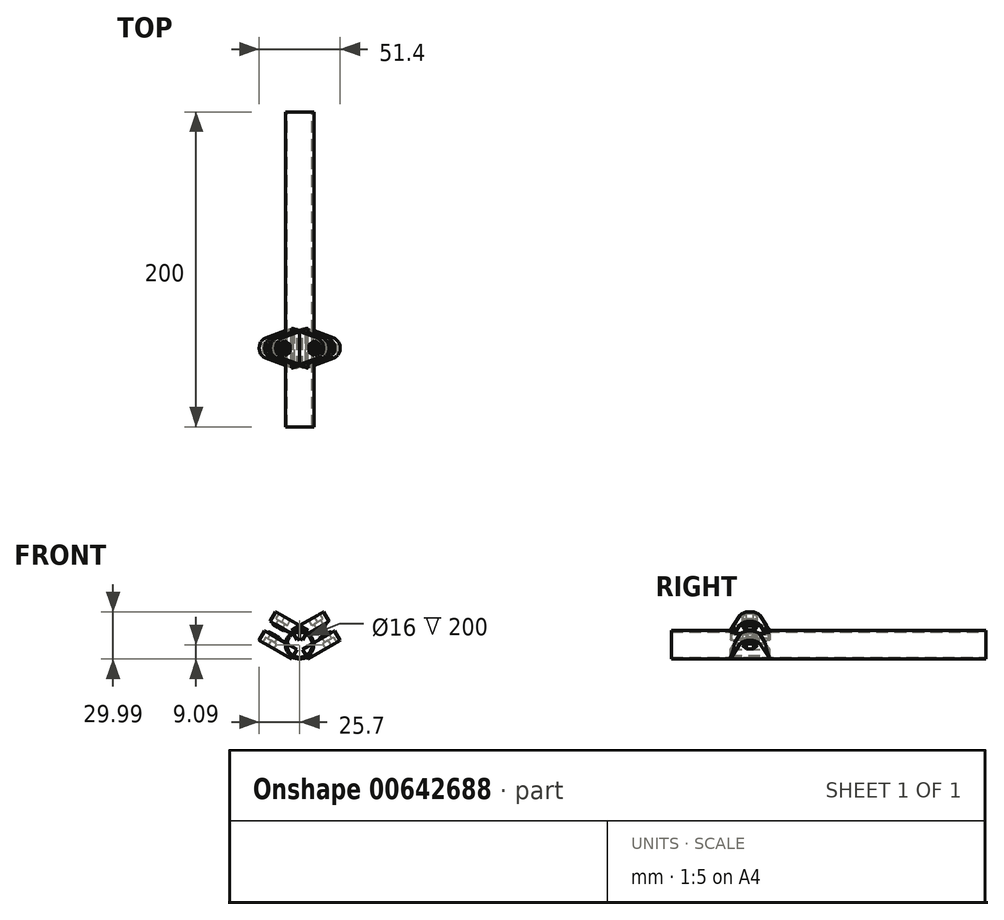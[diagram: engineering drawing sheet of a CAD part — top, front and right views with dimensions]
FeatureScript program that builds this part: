
annotation { "Feature Type Name" : "Feature", "Feature Type Description" : "" }
export const myFeature = defineFeature(function(context is Context, id is Id, definition is map)
    precondition{}
    {
        {
            var Q0;
            Q0=qCreatedBy(makeId("Front.planeOp"),FACE);
            var sketch = newSketch(context, id + "F0", { "sketchPlane" : qUnion([Q0])});
            skCircle(sketch, "E0", {"center": v(0, 0) * mm, "radius": 9 * mm});
            skCircle(sketch, "E1.0", {"center": v(0, 0) * mm, "radius": 8 * mm});
            skLineSegment(sketch, "E2", {"start": v(0, -17) * mm, "end": v(0, 17) * mm, "construction": true});
            skLineSegment(sketch, "E3", {"start": v(-22.42, 0) * mm, "end": v(22.42, 0) * mm, "construction": true});
            skLineSegment(sketch, "E4.bottom", {"start": v(2.5, -9) * mm, "end": v(-2.5, -9) * mm, "construction": true});
            skLineSegment(sketch, "E4.top", {"start": v(2.5, -25) * mm, "end": v(-2.5, -25) * mm, "construction": true});
            skLineSegment(sketch, "E4.left", {"start": v(2.5, -9) * mm, "end": v(2.5, -25) * mm, "construction": true});
            skLineSegment(sketch, "E4.right", {"start": v(-2.5, -9) * mm, "end": v(-2.5, -25) * mm, "construction": true});
            skPoint(sketch, "E4.middle", {"position": v(0, -17) * mm});
            skLineSegment(sketch, "E5", {"start": v(-2.5, -17) * mm, "end": v(2.5, -17) * mm, "construction": true});
            skLineSegment(sketch, "E6.1.0", {"start": v(-9.04, 2.33) * mm, "end": v(-6.54, 6.67) * mm, "construction": true});
            skLineSegment(sketch, "E6.1.1", {"start": v(-9.04, 2.33) * mm, "end": v(-22.9, 10.33) * mm, "construction": true});
            skLineSegment(sketch, "E6.1.2", {"start": v(-6.54, 6.67) * mm, "end": v(-20.4, 14.67) * mm, "construction": true});
            skLineSegment(sketch, "E6.1.3", {"start": v(-13.47, 10.67) * mm, "end": v(-15.97, 6.33) * mm, "construction": true});
            skLineSegment(sketch, "E6.1.4", {"start": v(-22.9, 10.33) * mm, "end": v(-20.4, 14.67) * mm, "construction": true});
            skLineSegment(sketch, "E6.2.0", {"start": v(6.54, 6.67) * mm, "end": v(9.04, 2.33) * mm, "construction": true});
            skLineSegment(sketch, "E6.2.1", {"start": v(6.54, 6.67) * mm, "end": v(20.4, 14.67) * mm, "construction": true});
            skLineSegment(sketch, "E6.2.2", {"start": v(9.04, 2.33) * mm, "end": v(22.9, 10.33) * mm, "construction": true});
            skLineSegment(sketch, "E6.2.3", {"start": v(15.97, 6.33) * mm, "end": v(13.47, 10.67) * mm, "construction": true});
            skLineSegment(sketch, "E6.2.4", {"start": v(20.4, 14.67) * mm, "end": v(22.9, 10.33) * mm, "construction": true});
            skLineSegment(sketch, "E6.anchor1", {"start": v(0, 0) * mm, "end": v(-2.5, -9) * mm, "construction": true});
            skLineSegment(sketch, "E6.anchor2", {"start": v(0, 0) * mm, "end": v(9.04, 2.33) * mm, "construction": true});
            skLineSegment(sketch, "E7", {"start": v(-21.65, 12.5) * mm, "end": v(-7.8, 4.5) * mm, "construction": true});
            skSolve(sketch);
        }
        {
            var Q0;
            Q0=qCreatedBy(makeId("Top.planeOp"),FACE);
            var sketch = newSketch(context, id + "F1", { "sketchPlane" : qUnion([Q0])});
            skPoint(sketch, "E8.0", {"position": v(0, 0) * mm});
            skLineSegment(sketch, "E9", {"start": v(0, -86.54) * mm, "end": v(0, 86.54) * mm, "construction": true});
            skSolve(sketch);
        }
        {
            var Q0;
            Q0 = qSketchRegion(id + "F0", true);
            extrude(context, id + "F2", {"entities" : qUnion([Q0]), "endBound" : BoundingType.SYMMETRIC, "depth" : 200 * mm, "offsetDistance" : 25 * mm});
        }
        {
            var Q0;
            Q0=qCreatedBy(makeId("Top.planeOp"),FACE);
            var Q1;
            Q1=sQuery(id+"F0.wireOp",EDGE,"E7");
            cPlane(context, id + "F3", {"entities" : qUnion([Q0, Q1]), "cplaneType" : CPlaneType.LINE_ANGLE, "offset" : 25 * mm, "angle" : 0 * degree, "width" : 150 * mm, "height" : 150 * mm});
        }
        {
            var Q0;
            Q0=qCreatedBy(makeId("Front.planeOp"),FACE);
            cPlane(context, id + "F4", {"entities" : qUnion([Q0]), "cplaneType" : CPlaneType.OFFSET, "offset" : 50 * mm, "width" : 150 * mm, "height" : 150 * mm});
        }
        {
            var Q0;
            Q0=qCreatedBy(id+"F3.planeOp",FACE);
            var sketch = newSketch(context, id + "F5", { "sketchPlane" : qUnion([Q0])});
            skLineSegment(sketch, "E10.0", {"start": v(0, 86.54) * mm, "end": v(0, -86.54) * mm, "construction": true});
            skLineSegment(sketch, "E11.0", {"start": v(-9, 0) * mm, "end": v(9, 0) * mm, "construction": true});
            skPoint(sketch, "E12.0", {"position": v(-17, 0) * mm});
            skLineSegment(sketch, "E13", {"start": v(-17, 0) * mm, "end": v(-17, 50) * mm, "construction": true});
            skLineSegment(sketch, "E14", {"start": v(-9, 0) * mm, "end": v(-9, 50) * mm, "construction": true});
            skCircle(sketch, "E15", {"center": v(-17, 50) * mm, "radius": 8 * mm, "construction": true});
            skCircle(sketch, "E16", {"center": v(-17, 50) * mm, "radius": 2.5 * mm, "construction": true});
            skCircle(sketch, "E17", {"center": v(-17, 50) * mm, "radius": 4 * mm, "construction": true});
            skLineSegment(sketch, "E18.0", {"start": v(-21, 47.7) * mm, "end": v(-21, 52.3) * mm, "construction": true});
            skLineSegment(sketch, "E18.1", {"start": v(-21, 52.3) * mm, "end": v(-17, 54.62) * mm, "construction": true});
            skLineSegment(sketch, "E18.2", {"start": v(-17, 54.62) * mm, "end": v(-13, 52.3) * mm, "construction": true});
            skLineSegment(sketch, "E18.3", {"start": v(-13, 52.3) * mm, "end": v(-13, 47.7) * mm, "construction": true});
            skLineSegment(sketch, "E18.4", {"start": v(-13, 47.7) * mm, "end": v(-17, 45.38) * mm, "construction": true});
            skLineSegment(sketch, "E18.5", {"start": v(-17, 45.38) * mm, "end": v(-21, 47.7) * mm, "construction": true});
            skPoint(sketch, "E18.0.midPoint", {"position": v(-21, 50) * mm});
            skSolve(sketch);
        }
        {
            var Q0;
            Q0=qCreatedBy(id+"F3.planeOp",FACE);
            var Q1;
            Q1=sQuery(id+"F0.wireOp",VERTEX,"E6.1.3.end");
            cPlane(context, id + "F6", {"entities" : qUnion([Q0, Q1]), "cplaneType" : CPlaneType.PLANE_POINT, "offset" : 25 * mm, "width" : 150 * mm, "height" : 150 * mm});
        }
        {
            var Q0;
            Q0=qCreatedBy(id+"F6.planeOp",FACE);
            cPlane(context, id + "F7", {"entities" : qUnion([Q0]), "cplaneType" : CPlaneType.OFFSET, "offset" : 1 * mm, "width" : 150 * mm, "height" : 150 * mm});
        }
        {
            var Q0;
            Q0=qCreatedBy(id+"F7.planeOp",FACE);
            var sketch = newSketch(context, id + "F8", { "sketchPlane" : qUnion([Q0])});
            skCircle(sketch, "E19.0", {"center": v(-17, 50) * mm, "radius": 2.5 * mm, "construction": true});
            skCircle(sketch, "E20.0", {"center": v(-17, 50) * mm, "radius": 4 * mm, "construction": true});
            skCircle(sketch, "E21.0", {"center": v(-17, 50) * mm, "radius": 8 * mm, "construction": true});
            skLineSegment(sketch, "E22.0", {"start": v(0, 86.54) * mm, "end": v(0, -86.54) * mm, "construction": true});
            skLineSegment(sketch, "E23.0", {"start": v(-21, 47.7) * mm, "end": v(-21, 52.3) * mm, "construction": true});
            skLineSegment(sketch, "E24.0", {"start": v(-21, 52.3) * mm, "end": v(-17, 54.62) * mm, "construction": true});
            skLineSegment(sketch, "E25.0", {"start": v(-17, 54.62) * mm, "end": v(-13, 52.3) * mm, "construction": true});
            skLineSegment(sketch, "E26.0", {"start": v(-13, 52.3) * mm, "end": v(-13, 47.7) * mm, "construction": true});
            skLineSegment(sketch, "E27.0", {"start": v(-13, 47.7) * mm, "end": v(-17, 45.38) * mm, "construction": true});
            skLineSegment(sketch, "E28.0", {"start": v(-17, 45.38) * mm, "end": v(-21, 47.7) * mm, "construction": true});
            skCircle(sketch, "E29", {"center": v(-17, 50) * mm, "radius": 6.62 * mm});
            skCircle(sketch, "E30", {"center": v(-17, 50) * mm, "radius": 4.62 * mm, "construction": true});
            skLineSegment(sketch, "E31", {"start": v(0, 62.56) * mm, "end": v(-19.07, 56.29) * mm});
            skLineSegment(sketch, "E32", {"start": v(0, 37.44) * mm, "end": v(-19.07, 43.71) * mm});
            skLineSegment(sketch, "E33", {"start": v(-17, 50) * mm, "end": v(0, 50) * mm, "construction": true});
            skLineSegment(sketch, "E34", {"start": v(0, 62.56) * mm, "end": v(0, 37.44) * mm});
            skCircle(sketch, "E35", {"center": v(-17, 50) * mm, "radius": 4.5 * mm});
            skSolve(sketch);
        }
        {
            var Q0;
            {var subQ0=sQuery(id+"F8.wireOp",EDGE,"E31");Q0=makeQuery(id+"F8.imprint","IMPRINT",FACE,{"disambiguationData":[TD([[makeQuery(id+"F8.imprint","IMPRINT",EDGE,{"derivedFrom":subQ0}),1.0]])]});}
            var Q1;
            Q1=makeQuery(id+"F8.imprint","IMPRINT",FACE,{"disambiguationData":[TD([[makeQuery(id+"F8.imprint","IMPRINT",EDGE,{"derivedFrom":sQuery(id+"F8.wireOp",EDGE,"E35")}),-1.0]])]});
            var Q2;
            Q2=makeQuery(id+"F8.imprint","IMPRINT",FACE,{"disambiguationData":[TD([[makeQuery(id+"F8.imprint","IMPRINT",EDGE,{"derivedFrom":sQuery(id+"F8.wireOp",EDGE,"E35")}),1.0]])]});
            extrude(context, id + "F9", {"entities" : qUnion([Q0, Q1, Q2]), "depth" : 7 * mm, "offsetDistance" : 25 * mm});
        }
        {
            var Q0;
            Q0=qCreatedBy(id+"F6.planeOp",FACE);
            var sketch = newSketch(context, id + "F10", { "sketchPlane" : qUnion([Q0])});
            skCircle(sketch, "E36.0", {"center": v(-17, 50) * mm, "radius": 2.5 * mm, "construction": true});
            skCircle(sketch, "E37", {"center": v(-17, 50) * mm, "radius": 3.8 * mm});
            skSolve(sketch);
        }
        {
            var Q1;
            Q1=makeQuery(id+"F8.imprint","IMPRINT",FACE,{"disambiguationData":[TD([[makeQuery(id+"F8.imprint","IMPRINT",EDGE,{"derivedFrom":sQuery(id+"F8.wireOp",EDGE,"E35")}),1.0]])]});
            var Q2;
            Q2=makeQuery(id+"F10.imprint","IMPRINT",FACE,{"disambiguationData":[TD([[makeQuery(id+"F10.imprint","IMPRINT",EDGE,{"derivedFrom":sQuery(id+"F10.wireOp",EDGE,"E37")}),1.0]])]});
            loft(context, id + "F11", {"operationType" : NewBodyOperationType.ADD, "sheetProfilesArray" : [{ "sheetProfileEntities" : qUnion([Q1]) }, { "sheetProfileEntities" : qUnion([Q2]) }]});
        }
        {
            var Q0;
            Q0=makeQuery(id+"F9.opExtrude","CAP_FACE",FACE,{"disambiguationData":[OSD([sQuery(id+"F8.wireOp",EDGE,"E29"),sQuery(id+"F8.wireOp",EDGE,"E31"),sQuery(id+"F8.wireOp",EDGE,"E32"),sQuery(id+"F8.wireOp",EDGE,"E34")])],"isStart":false});
            var sketch = newSketch(context, id + "F12", { "sketchPlane" : qUnion([Q0])});
            skPoint(sketch, "E38.0", {"position": v(-17, 50) * mm});
            skCircle(sketch, "E39.cCircle", {"center": v(-17, 50) * mm, "radius": 4.05 * mm, "construction": true});
            skLineSegment(sketch, "E39.0", {"start": v(-21.05, 47.66) * mm, "end": v(-21.05, 52.34) * mm});
            skLineSegment(sketch, "E39.1", {"start": v(-21.05, 52.34) * mm, "end": v(-17, 54.68) * mm});
            skLineSegment(sketch, "E39.2", {"start": v(-17, 54.68) * mm, "end": v(-12.95, 52.34) * mm});
            skLineSegment(sketch, "E39.3", {"start": v(-12.95, 52.34) * mm, "end": v(-12.95, 47.66) * mm});
            skLineSegment(sketch, "E39.4", {"start": v(-12.95, 47.66) * mm, "end": v(-17, 45.32) * mm});
            skLineSegment(sketch, "E39.5", {"start": v(-17, 45.32) * mm, "end": v(-21.05, 47.66) * mm});
            skPoint(sketch, "E39.0.midPoint", {"position": v(-21.05, 50) * mm});
            skSolve(sketch);
        }
        {
            var Q0;
            Q0=sQuery(id+"F12.wireOp",VERTEX,"E38.0");
            var Q1;
            Q1=makeQuery(id+"F9.opExtrude","SWEPT_BODY",BODY,{"disambiguationData":[OSD([sQuery(id+"F8.wireOp",EDGE,"E29"),sQuery(id+"F8.wireOp",EDGE,"E31"),sQuery(id+"F8.wireOp",EDGE,"E32"),sQuery(id+"F8.wireOp",EDGE,"E34")])]});
            hole(context, id + "F13", {"style" : HoleStyle.SIMPLE, "endStyle" : HoleEndStyle.THROUGH, "holeDiameter" : 5 * mm, "majorDiameter" : 5 * mm, "isTappedThrough" : true, "tappedDepth" : 12 * mm, "tapClearance" : 3, "startFromSketch" : true, "locations" : qUnion([Q0]), "scope" : qUnion([Q1])});
        }
        {
            var Q0;
            Q0=makeQuery(id+"F12.imprint","IMPRINT",FACE,{"disambiguationData":[TD([[makeQuery(id+"F12.imprint","IMPRINT",EDGE,{"derivedFrom":sQuery(id+"F12.wireOp",EDGE,"E39.0")}),-1.0]])]});
            extrude(context, id + "F14", {"entities" : qUnion([Q0]), "operationType" : NewBodyOperationType.REMOVE, "oppositeDirection" : true, "depth" : 3.75 * mm, "offsetDistance" : 25 * mm});
        }
        {
            var Q0;
            Q0=makeQuery(id+"F9.opExtrude","SWEPT_BODY",BODY,{"disambiguationData":[OSD([sQuery(id+"F8.wireOp",EDGE,"E29"),sQuery(id+"F8.wireOp",EDGE,"E31"),sQuery(id+"F8.wireOp",EDGE,"E32"),sQuery(id+"F8.wireOp",EDGE,"E34")])]});
            var Q1;
            Q1=qCreatedBy(id+"F3.planeOp",FACE);
            mirror(context, id + "F15", {"entities" : qUnion([Q0]), "mirrorPlane" : qUnion([Q1])});
        }
        {
            var Q0;
            Q0=makeQuery(id+"F9.opExtrude","SWEPT_BODY",BODY,{"disambiguationData":[OSD([sQuery(id+"F8.wireOp",EDGE,"E29"),sQuery(id+"F8.wireOp",EDGE,"E31"),sQuery(id+"F8.wireOp",EDGE,"E32"),sQuery(id+"F8.wireOp",EDGE,"E34")])]});
            var Q1;
            Q1=makeQuery(id+"F15.opPattern","COPY",BODY,{"derivedFrom":makeQuery(id+"F9.opExtrude","SWEPT_BODY",BODY,{"disambiguationData":[OSD([sQuery(id+"F8.wireOp",EDGE,"E29"),sQuery(id+"F8.wireOp",EDGE,"E31"),sQuery(id+"F8.wireOp",EDGE,"E32"),sQuery(id+"F8.wireOp",EDGE,"E34")])]}),"instanceName":"1"});
            var Q2;
            Q2=qCreatedBy(makeId("Right.planeOp"),FACE);
            mirror(context, id + "F16", {"operationType" : NewBodyOperationType.ADD, "entities" : qUnion([Q0, Q1]), "mirrorPlane" : qUnion([Q2])});
        }
    });
